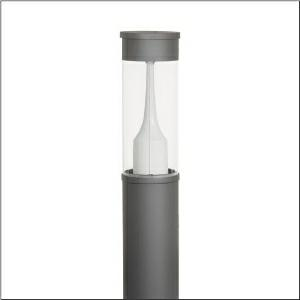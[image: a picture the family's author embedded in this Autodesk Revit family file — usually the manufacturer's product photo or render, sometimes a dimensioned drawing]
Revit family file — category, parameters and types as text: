
# Revit family: city-light_400_iq___st1_2a_5xa5305kf14h_7e7c
name_source: partatom
category: Lighting Fixtures
units: mm (PartAtom-declared; Revit-internal decimal feet)

## family parameters
Cut with Voids When Loaded = No
Host = Face
Light Source = No
Part Type = Normal
Room Calculation Point = No
Round Connector Dimension = Use Diameter
Shared = No

## types (1)
- --- (1 x LED, 1540 lm, 10 W, 4000K)
    Apparent Load = 10 VA
    CIE Flux Codes = 22 61 93 96 100
    Color Rendering = 70
    Color Temperature = 4000K
    Default Elevation = 1800 mm
    Description = City-Light 400 iQ, light pillar, Module 540 iQ-SR, primary light control with 3 zone facetted reflector, of plastic, silver coated, highly specular, structured, primary optical cover: cover, of PMMA, transparent, partly coated, light distribution: ST1.2a, primary light characteristic: asymmetric, LED, High Power LED, rated luminous flux: 1.540lm, luminous efficacy: 154lm/W, light colour: 740, colour temperature: 4000K, control gear: iQ Street-Remote, control: pre-setting: logarithmic dimming characteristic, Street-Remote, Auto-Match, Temp-Guard, Lumen-Switch, Night-Set, Smart-Wire, Light-Fading, Desk-Remote (wireless, voltage-free reading and setting of iQ features in the workshop via application-optimized NFC function/RFID function), optimised constant luminous flux control (CLO 2.0), with terminal, 6-pole, max. 2.5mm², mains connection: 230..240V, AC, 50/60Hz, start of lifetime: 10W, end of service life: 10W, reduction: 5W, luminaire housing, cylindrical, of extruded aluminium section, coated, Siteco® metallic grey (DB 702S), length: 4.694mm, diameter: 200mm, Module 540 iQ-SR, traffic white (RAL 9016), equipment: standard, protection rating (complete): IP65, insulation class (complete): insulation class II (safety insulation), certification: CE, ENEC, VDE, packaging unit: 1 piece

Light Distribution: ST1.2a
    Height = 500 mm
    Lamp = 1 x LED
    Lamp Light Flux = 1540 lm
    Lamp Power = 10 W
    Lamp count = 1
    Length = 200 mm  [stored 0.656168 ft]
    Luminous efficacy = 154 lm/W
    Manufacturer = Siteco
    ModVariant = No
    Model = 5XA5305KF14H
    Mounting Place = Floor
    Mounting Type = Freestanding
    Number of Poles = 1
    OnlyDefault = Yes
    Power Factor = 1
    Product Name = City-Light 400 iQ | ST1.2a
    Product group = light pillar
    ProductGroupID = 1301
    Protection Class = Protection class II
    Protection Degree = IP 65
    RLX_Detail_Level = 1
    RLX_Emergency_Light_Flux = 0 lm
    RLX_Emergency_Type = 0
    RLX_Emergency_Type_DB = No
    RlxData = <blob elided: 87893 chars, md5=c936d38d>
    Socket = socket
    Standby Power = 0 W
    System Light Flux = 1540 lm
    System Power = 10 W
    Type Comments = factory setting: luminous flux: 100 % | dim-lin: 254 | 401 mA
    Type Image = l_1006914.jpg
    URL = http://relux.com
    VarID = @adj_159098
    Voltage = 0 V
    Weight = 0.00 kg
    Width = 0 mm  [stored 0 ft]

note: [stored X ft] marks values corroborated as IEEE doubles in the binary element streams (Revit-internal decimal feet)

## geometry (parser evidence)
native form markers: Blend x4, Sweep x11
no freeform markers — native parametric forms only
